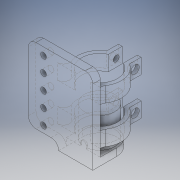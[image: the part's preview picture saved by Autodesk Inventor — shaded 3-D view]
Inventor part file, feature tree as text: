
AUTODESK INVENTOR PART (.ipt)
format: ipt  version: 2018 (Build 220112000, 112)  size: 289,792 bytes
history: native  units: in
note: dims shown in document units (in); Inventor stores cm internally (conversion verified against a paired STEP export)
features: extrude x8, sketch x8, fillet x4, plane x2, pattern_linear x1
ambient origin geometry x8: Origin, YZ Plane, XZ Plane, XY Plane, X Axis, Y Axis, Z Axis, Center Point
bodies: Solid1 (feature_tree)
feature tree (23):
  extrude  "Extrusion1"  Depth=1.0in TaperAngle=0.0deg
  plane  "Work Plane1"
  extrude  "Extrusion2"  Depth=0.5in
  extrude  "Extrusion3"  Depth=0.0984in
  extrude  "Extrusion4"  Depth=0.0787in TaperAngle=0.0deg
  plane  "Work Plane2"
  extrude  "Extrusion5"  Depth=0.25in TaperAngle=0.0deg
  pattern_linear  "Rectangular Pattern1"  Spacing1=0.0625in  [1 undecoded]
  extrude  "Extrusion6"  Depth=1.125in
  extrude  "Extrusion7"  Depth=0.25in
  fillet  "Fillet1"  Radius=2.471in
  extrude  "Extrusion8"  [1 undecoded]
  fillet  "Fillet2"  Radius=0.6729in
  fillet  "Fillet3"  Radius=0.7573in
  fillet  "Fillet4"  Radius=0.1875in
  sketch  "Sketch1"  dims[d0=1.0in d1=1.0in d2=0.0in]
  sketch  "Sketch3"  dims[d3=0.5in d8=0.0945in]
  sketch  "Sketch4"  dims[d9=0.1969in d10=0.0984in]
  sketch  "Sketch5"  dims[d11=0.0945in d12=0.0787in d13=0.0in]
  sketch  "Sketch6"  dims[d14=0.25in d15=0.25in d16=0.0in]
  sketch  "Sketch7"  dims[d17=1.125in]
  sketch  "Sketch8"  dims[d18=0.5625in]
  sketch  "Sketch9"  dims[d19=0.5625in d20=0.0625in d21=1.125in d22=0.25in d23=2.471in d24=0.0in d25=-0.75in d26=1.19in d27=0.125in d28=0.375in d29=1.0in d30=0.125in d31=0.6729in d32=0.7573in d33=0.1875in d34=0.1856in d35=0.3106in d36=0.425in d37=0.55in d38=0.5in d39=0.0in d40=0.7874in d42=1.25in d43=0.194in d44=0.194in d45=0.25in d46=0.25in d47=0.2in d48=0.2in d49=0.5in d50=0.0in d51=0.274in d52=0.274in d53=0.5in d54=0.0in d55=0.2in d56=0.1935in d57=0.5in d59=0.5in d60=0.5in d61=0.5in d64=0.1935in d65=0.1935in d66=0.1935in d67=0.1935in d71=0.25in d72=0.0in d73=2.125in d74=0.5394in d75=0.5in d76=0.25in d77=0.5in d78=0.5in d79=0.5in d80=0.5in d81=0.25in d82=0.25in d83=0.25in]
note: 2 required parameter values undecoded (feature->parameter linkage not recoverable at this tier; creation-order binding heuristic only, values carry confidence <= 0.55)
